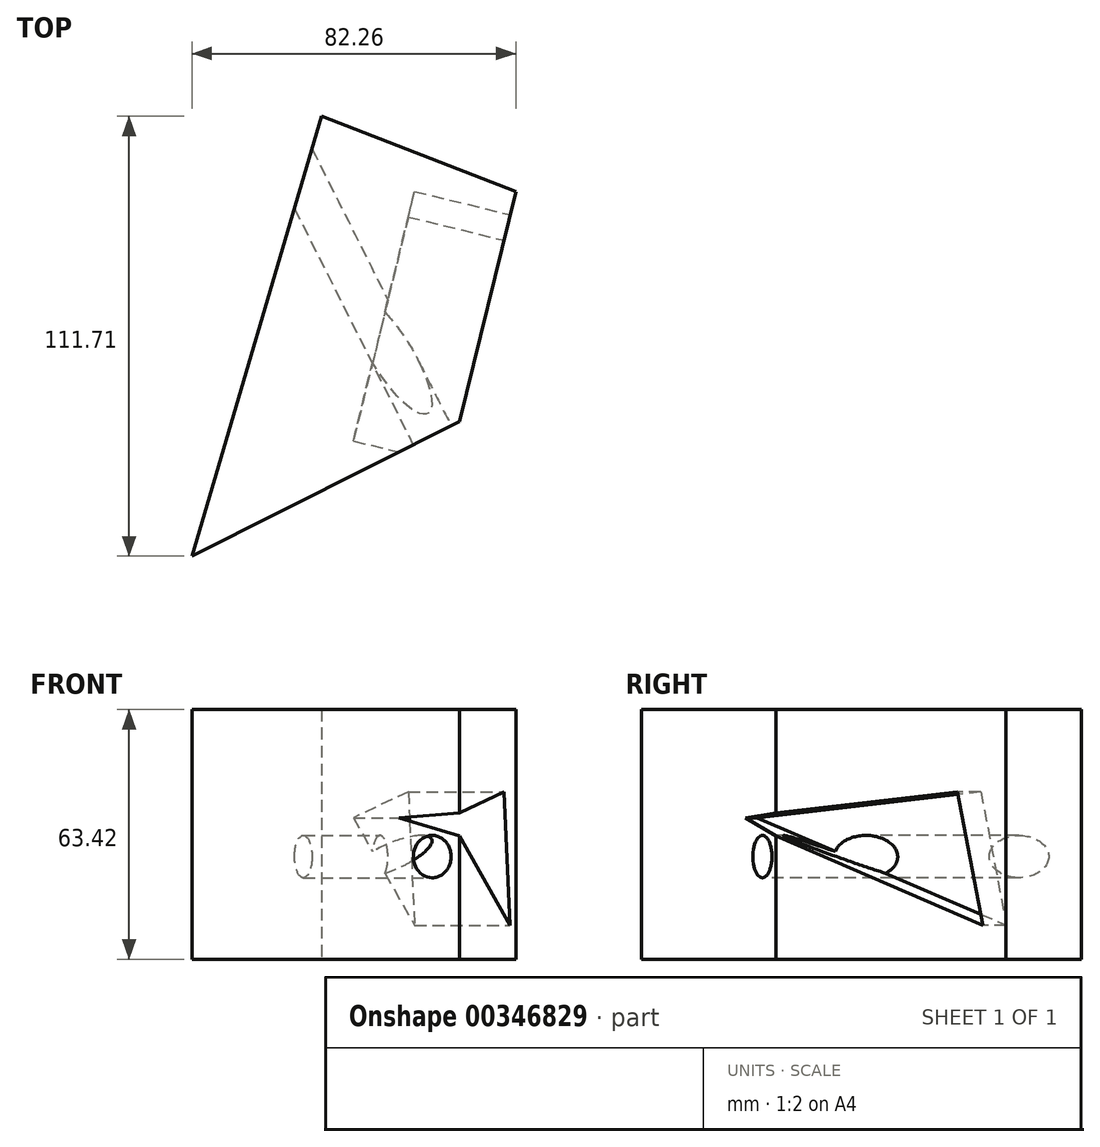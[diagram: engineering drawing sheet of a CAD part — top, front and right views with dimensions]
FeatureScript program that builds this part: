
annotation { "Feature Type Name" : "Feature", "Feature Type Description" : "" }
export const myFeature = defineFeature(function(context is Context, id is Id, definition is map)
    precondition{}
    {
        {
            var Q0;
            Q0=qCreatedBy(makeId("Top.planeOp"),FACE);
            var sketch = newSketch(context, id + "F0", { "sketchPlane" : qUnion([Q0])});
            skLineSegment(sketch, "E0", {"start": v(34.98, -14.25) * mm, "end": v(-32.96, -48.38) * mm});
            skLineSegment(sketch, "E1", {"start": v(-32.96, -48.38) * mm, "end": v(0, 63.33) * mm});
            skLineSegment(sketch, "E2", {"start": v(49.3, 44.17) * mm, "end": v(0, 63.33) * mm});
            skLineSegment(sketch, "E3", {"start": v(34.98, -14.25) * mm, "end": v(49.3, 44.17) * mm});
            skSolve(sketch);
        }
        {
            var Q0;
            Q0 = qSketchRegion(id + "F0", true);
            extrude(context, id + "F1", {"entities" : qUnion([Q0]), "depth" : 63.42 * mm});
        }
        {
            var Q0;
            Q0=makeQuery(id+"F1.opExtrude","SWEPT_FACE",FACE,{"disambiguationData":[OSD([sQuery(id+"F0.wireOp",EDGE,"E0")])]});
            var sketch = newSketch(context, id + "F2", { "sketchPlane" : qUnion([Q0])});
            skCircle(sketch, "E4", {"center": v(17.12, 26.05) * mm, "radius": 5.39 * mm});
            skSolve(sketch);
        }
        {
            var Q0;
            Q0 = qSketchRegion(id + "F2", true);
            extrude(context, id + "F3", {"entities" : qUnion([Q0]), "operationType" : NewBodyOperationType.REMOVE, "oppositeDirection" : true, "depth" : 102.12 * mm});
        }
        {
            var Q0;
            Q0=makeQuery(id+"F1.opExtrude","SWEPT_FACE",FACE,{"disambiguationData":[OSD([sQuery(id+"F0.wireOp",EDGE,"E3")])]});
            var sketch = newSketch(context, id + "F4", { "sketchPlane" : qUnion([Q0])});
            skSolve(sketch);
        }
        {
            var Q0;
            {var subQ0=sQuery(id+"F0.wireOp",EDGE,"E3");Q0=makeQuery(id+"F4.imprint","IMPRINT",FACE,{"disambiguationData":[TD([[makeQuery(id+"F4.imprint","IMPRINT",EDGE,{"derivedFrom":makeQuery(id+"F1.opExtrude","CAP_EDGE",EDGE,{"disambiguationData":[OSD([subQ0])],"isStart":true})}),1.0]])]});}
            var sketch = newSketch(context, id + "F5", { "sketchPlane" : qUnion([Q0])});
            skLineSegment(sketch, "E5", {"start": v(41.94, 42.48) * mm, "end": v(-16.68, 35.94) * mm});
            skLineSegment(sketch, "E6", {"start": v(41.94, 42.48) * mm, "end": v(48.61, 8.59) * mm});
            skLineSegment(sketch, "E7", {"start": v(-16.68, 35.94) * mm, "end": v(48.61, 8.59) * mm});
            skSolve(sketch);
        }
        {
            var Q0;
            Q0 = qSketchRegion(id + "F5", true);
            extrude(context, id + "F6", {"entities" : qUnion([Q0]), "operationType" : NewBodyOperationType.REMOVE, "oppositeDirection" : true, "depth" : 25 * mm});
        }
    });
